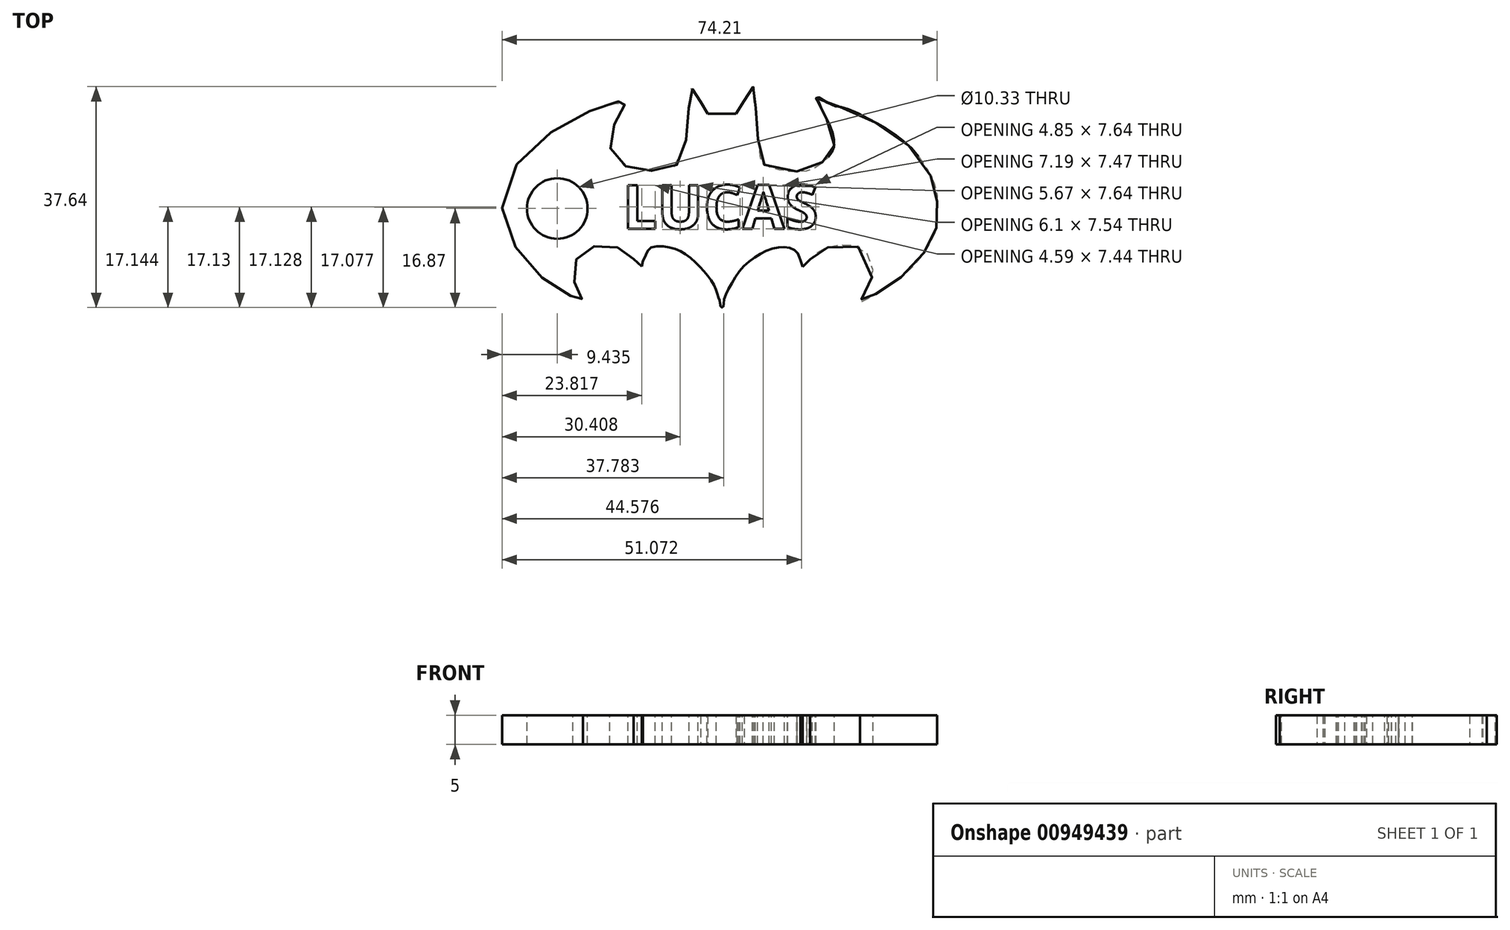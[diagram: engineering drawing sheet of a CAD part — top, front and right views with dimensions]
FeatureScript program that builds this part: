
annotation { "Feature Type Name" : "Feature", "Feature Type Description" : "" }
export const myFeature = defineFeature(function(context is Context, id is Id, definition is map)
    precondition{}
    {
        {
            var Q0;
            Q0=qCreatedBy(makeId("Top.planeOp"),FACE);
            var sketch = newSketch(context, id + "F0", { "sketchPlane" : qUnion([Q0])});
            skLineSegment(sketch, "E0", {"start": v(17.66, -46.63) * mm, "end": v(17.66, -46.63) * mm});
            skLineSegment(sketch, "E1", {"start": v(-27, -17.85) * mm, "end": v(-27.41, -19.78) * mm});
            skLineSegment(sketch, "E2", {"start": v(-27.41, -19.78) * mm, "end": v(-30.25, -17.16) * mm});
            skLineSegment(sketch, "E3", {"start": v(-7.41, 36.4) * mm, "end": v(-4.97, 32.28) * mm});
            skLineSegment(sketch, "E4", {"start": v(-4.97, 32.28) * mm, "end": v(-0.1, 32.28) * mm});
            skLineSegment(sketch, "E5", {"start": v(-0.1, 32.28) * mm, "end": v(4.75, 32.28) * mm});
            skLineSegment(sketch, "E6", {"start": v(4.75, 32.28) * mm, "end": v(7.5, 36.75) * mm});
            skLineSegment(sketch, "E7", {"start": v(30, -17.28) * mm, "end": v(27.37, -19.85) * mm});
            skLineSegment(sketch, "E8", {"start": v(27.37, -19.85) * mm, "end": v(26.62, -17.56) * mm});
            skFitSpline(sketch, "E9", {"points": [v(-0.67, -32.74) * mm, v(-0.72, -32.42) * mm, v(-0.87, -31.55) * mm, v(-1.37, -30.07) * mm, v(-2.33, -27.07) * mm, v(-4.94, -22.95) * mm, v(-9.05, -18.48) * mm, v(-14.03, -14.66) * mm, v(-19.36, -13.03) * mm, v(-24.89, -13.72) * mm, v(-26.32, -16.53) * mm, v(-27, -17.85) * mm]});
            skFitSpline(sketch, "E10", {"points": [v(-30.25, -17.16) * mm, v(-31.32, -16.23) * mm, v(-33.31, -14.5) * mm, v(-36.97, -12.95) * mm, v(-40.69, -12.62) * mm, v(-44.31, -13.01) * mm, v(-47.44, -14.64) * mm, v(-49.65, -17.2) * mm, v(-50.84, -20.46) * mm, v(-50.62, -24.2) * mm, v(-49.5, -27.18) * mm, v(-48.4, -29.54) * mm, v(-48.02, -30.57) * mm, v(-47.58, -31.82) * mm, v(-49.28, -30.8) * mm, v(-50.74, -30.2) * mm, v(-56.1, -27.22) * mm, v(-63.04, -22.25) * mm, v(-70.18, -13.6) * mm, v(-74.82, -3) * mm, v(-72.99, 10.16) * mm, v(-63.13, 22.49) * mm, v(-52.35, 29.54) * mm, v(-41.97, 34.29) * mm, v(-38.1, 34.92) * mm, v(-32.3, 38.2) * mm, v(-32.67, 36.4) * mm, v(-33.2, 35.53) * mm, v(-34.45, 33.52) * mm, v(-36.13, 30.4) * mm, v(-37.47, 26.28) * mm, v(-38.38, 22.42) * mm, v(-37.45, 18.9) * mm, v(-35.16, 16.14) * mm, v(-31.8, 13.79) * mm, v(-27.1, 12.95) * mm, v(-22.18, 12.98) * mm, v(-17.66, 13.92) * mm, v(-14.03, 16.16) * mm, v(-12.47, 21.01) * mm, v(-12.14, 27.18) * mm, v(-11.4, 34.27) * mm, v(-11.17, 37.8) * mm, v(-10.47, 40.95) * mm, v(-9.46, 39.55) * mm, v(-8.6, 38.36) * mm, v(-7.85, 37.1) * mm, v(-7.41, 36.4) * mm]});
            skFitSpline(sketch, "E11", {"points": [v(7.5, 36.75) * mm, v(8, 37.51) * mm, v(8.82, 38.82) * mm, v(9.65, 40.08) * mm, v(10.8, 41.53) * mm, v(10.58, 37.79) * mm, v(11.3, 35.16) * mm, v(11.59, 29.4) * mm, v(12.12, 24.17) * mm, v(12.7, 20.02) * mm, v(13.41, 15.78) * mm, v(18.9, 13.43) * mm, v(25.3, 12.64) * mm, v(30.97, 13.56) * mm, v(33.99, 15.64) * mm, v(35.43, 16.9) * mm, v(37.1, 18.74) * mm, v(38.2, 22) * mm, v(37.29, 26.83) * mm, v(35.45, 30.9) * mm, v(33.74, 34.33) * mm, v(33.03, 35.91) * mm, v(32.02, 38.08) * mm, v(37.64, 35.16) * mm, v(41.14, 34.44) * mm, v(49.27, 30.9) * mm, v(57.38, 26.28) * mm, v(65.7, 19.27) * mm, v(70.2, 12.7) * mm, v(72.62, 7.85) * mm, v(73.29, 4.1) * mm, v(73.16, -0.06) * mm, v(73.29, -4.23) * mm, v(72.62, -7.97) * mm, v(70.68, -11.85) * mm, v(67.75, -16.6) * mm, v(63.1, -21.63) * mm, v(58.28, -25.46) * mm, v(53.23, -28.82) * mm, v(50.78, -29.8) * mm, v(47.1, -32.52) * mm, v(47.5, -31.03) * mm, v(47.96, -30.06) * mm, v(49.6, -26.69) * mm, v(51.4, -21.29) * mm, v(48.02, -13.94) * mm, v(41.74, -12.45) * mm, v(36.8, -13) * mm, v(33.03, -14.55) * mm, v(31.05, -16.34) * mm, v(30, -17.28) * mm]});
            skFitSpline(sketch, "E12", {"points": [v(26.62, -17.56) * mm, v(26.27, -16.7) * mm, v(25.6, -15.05) * mm, v(23.13, -13.52) * mm, v(19.85, -13.21) * mm, v(15.83, -14.04) * mm, v(11.54, -16.33) * mm, v(7.47, -19.58) * mm, v(4.22, -23.85) * mm, v(1.82, -28) * mm, v(0.64, -31.17) * mm, v(0.55, -32.88) * mm, v(0.38, -33.43) * mm, v(-0.01, -33.74) * mm, v(-0.4, -33.55) * mm, v(-0.62, -33.2) * mm, v(-0.65, -32.9) * mm, v(-0.67, -32.74) * mm]});
            skSolve(sketch);
        }
        {
            var Q0;
            Q0=makeQuery(id+"F0.imprint","IMPRINT",FACE,{"disambiguationData":[TD([[makeQuery(id+"F0.imprint","IMPRINT",EDGE,{"derivedFrom":sQuery(id+"F0.wireOp",EDGE,"E1")}),-1.0]])]});
            extrude(context, id + "F1", {"entities" : qUnion([Q0]), "depth" : 10 * mm, "offsetDistance" : 25 * mm});
        }
        {
            var Q0;
            Q0=makeQuery(id+"F1.opExtrude","CAP_FACE",FACE,{"disambiguationData":[OSD([sQuery(id+"F0.wireOp",EDGE,"E1"),sQuery(id+"F0.wireOp",EDGE,"E2"),sQuery(id+"F0.wireOp",EDGE,"E3"),sQuery(id+"F0.wireOp",EDGE,"E4"),sQuery(id+"F0.wireOp",EDGE,"E5"),sQuery(id+"F0.wireOp",EDGE,"E6"),sQuery(id+"F0.wireOp",EDGE,"E7"),sQuery(id+"F0.wireOp",EDGE,"E8"),sQuery(id+"F0.wireOp",EDGE,"E9"),sQuery(id+"F0.wireOp",EDGE,"E10"),sQuery(id+"F0.wireOp",EDGE,"E11"),sQuery(id+"F0.wireOp",EDGE,"E12")])],"isStart":false});
            var sketch = newSketch(context, id + "F2", { "sketchPlane" : qUnion([Q0])});
            skText(sketch, "E13", { "text": "LUCAS", "fontName": "OpenSans-Bold.ttf"});
            const initialGuessF2  = {"E13": [-0.03395, -0.00692, 1, 0, 0.015]};
            skSetInitialGuess(sketch, initialGuessF2);
            skSolve(sketch);
        }
        {
            var Q0;
            Q0=makeQuery(id+"F2.imprint","IMPRINT",FACE,{"disambiguationData":[TD([[makeQuery(id+"F2.imprint","IMPRINT",EDGE,{"derivedFrom":sQuery(id+"F2.wireOp",EDGE,"E13.sketch_text.stroke-0")}),-1.0]])]});
            var Q1;
            Q1=makeQuery(id+"F2.imprint","IMPRINT",FACE,{"disambiguationData":[TD([[makeQuery(id+"F2.imprint","IMPRINT",EDGE,{"derivedFrom":sQuery(id+"F2.wireOp",EDGE,"E13.sketch_text.stroke-6")}),-1.0]])]});
            var Q2;
            Q2=makeQuery(id+"F2.imprint","IMPRINT",FACE,{"disambiguationData":[TD([[makeQuery(id+"F2.imprint","IMPRINT",EDGE,{"derivedFrom":sQuery(id+"F2.wireOp",EDGE,"E13.sketch_text.stroke-21")}),-1.0]])]});
            var Q3;
            Q3=makeQuery(id+"F2.imprint","IMPRINT",FACE,{"disambiguationData":[TD([[makeQuery(id+"F2.imprint","IMPRINT",EDGE,{"derivedFrom":sQuery(id+"F2.wireOp",EDGE,"E13.sketch_text.stroke-36")}),-1.0]])]});
            var Q4;
            Q4=makeQuery(id+"F2.imprint","IMPRINT",FACE,{"disambiguationData":[TD([[makeQuery(id+"F2.imprint","IMPRINT",EDGE,{"derivedFrom":sQuery(id+"F2.wireOp",EDGE,"E13.sketch_text.stroke-48")}),-1.0]])]});
            extrude(context, id + "F3", {"entities" : qUnion([Q0, Q1, Q2, Q3, Q4]), "operationType" : NewBodyOperationType.REMOVE, "oppositeDirection" : true, "depth" : 10 * mm, "offsetDistance" : 25 * mm});
        }
        {
            var Q0;
            {var subQ0=sQuery(id+"F0.wireOp",EDGE,"E10");var subQ1=sQuery(id+"F0.wireOp",EDGE,"E9");var subQ2=sQuery(id+"F0.wireOp",EDGE,"E8");var subQ3=sQuery(id+"F0.wireOp",EDGE,"E7");var subQ4=sQuery(id+"F0.wireOp",EDGE,"E6");var subQ5=sQuery(id+"F0.wireOp",EDGE,"E11");var subQ6=sQuery(id+"F0.wireOp",EDGE,"E1");var subQ7=sQuery(id+"F0.wireOp",EDGE,"E5");var subQ8=sQuery(id+"F0.wireOp",EDGE,"E4");var subQ9=sQuery(id+"F0.wireOp",EDGE,"E2");var subQ10=sQuery(id+"F0.wireOp",EDGE,"E3");var subQ11=sQuery(id+"F0.wireOp",EDGE,"E12");Q0=makeQuery(id+"F3.boolean.opBoolean","SPLIT",FACE,{"disambiguationData":[TD([makeQuery(id+"F1.opExtrude","SWEPT_FACE",FACE,{"disambiguationData":[OSD([subQ6])]})])],"derivedFrom":makeQuery(id+"F1.opExtrude","CAP_FACE",FACE,{"disambiguationData":[OSD([subQ6,subQ9,subQ10,subQ8,subQ7,subQ4,subQ3,subQ2,subQ1,subQ0,subQ5,subQ11])],"isStart":false})});}
            var sketch = newSketch(context, id + "F4", { "sketchPlane" : qUnion([Q0])});
            skCircle(sketch, "E14", {"center": v(-56.25, 0) * mm, "radius": 10.33 * mm});
            skSolve(sketch);
        }
        {
            var Q0;
            Q0=makeQuery(id+"F4.imprint","IMPRINT",FACE,{"disambiguationData":[TD([[makeQuery(id+"F4.imprint","IMPRINT",EDGE,{"derivedFrom":sQuery(id+"F4.wireOp",EDGE,"E14")}),1.0]])]});
            extrude(context, id + "F5", {"entities" : qUnion([Q0]), "operationType" : NewBodyOperationType.REMOVE, "oppositeDirection" : true, "depth" : 10 * mm, "offsetDistance" : 25 * mm});
        }
        {
            var Q0;
            Q0=makeQuery(id+"F3.boolean.opBoolean","SPLIT",BODY,{"disambiguationData":[OD(1.0)],"derivedFrom":makeQuery(id+"F1.opExtrude","SWEPT_BODY",BODY,{"disambiguationData":[OSD([sQuery(id+"F0.wireOp",EDGE,"E1"),sQuery(id+"F0.wireOp",EDGE,"E2"),sQuery(id+"F0.wireOp",EDGE,"E3"),sQuery(id+"F0.wireOp",EDGE,"E4"),sQuery(id+"F0.wireOp",EDGE,"E5"),sQuery(id+"F0.wireOp",EDGE,"E6"),sQuery(id+"F0.wireOp",EDGE,"E7"),sQuery(id+"F0.wireOp",EDGE,"E8"),sQuery(id+"F0.wireOp",EDGE,"E9"),sQuery(id+"F0.wireOp",EDGE,"E10"),sQuery(id+"F0.wireOp",EDGE,"E11"),sQuery(id+"F0.wireOp",EDGE,"E12")])]})});
            var Q1;
            Q1=makeQuery(id+"F3.boolean.opBoolean","SPLIT",BODY,{"disambiguationData":[OD(0.0)],"derivedFrom":makeQuery(id+"F1.opExtrude","SWEPT_BODY",BODY,{"disambiguationData":[OSD([sQuery(id+"F0.wireOp",EDGE,"E1"),sQuery(id+"F0.wireOp",EDGE,"E2"),sQuery(id+"F0.wireOp",EDGE,"E3"),sQuery(id+"F0.wireOp",EDGE,"E4"),sQuery(id+"F0.wireOp",EDGE,"E5"),sQuery(id+"F0.wireOp",EDGE,"E6"),sQuery(id+"F0.wireOp",EDGE,"E7"),sQuery(id+"F0.wireOp",EDGE,"E8"),sQuery(id+"F0.wireOp",EDGE,"E9"),sQuery(id+"F0.wireOp",EDGE,"E10"),sQuery(id+"F0.wireOp",EDGE,"E11"),sQuery(id+"F0.wireOp",EDGE,"E12")])]})});
            var Q2;
            Q2=qCreatedBy(makeId("Origin.pointOp"),VERTEX);
            transform(context, id + "F6", {"entities" : qUnion([Q0, Q1]), "transformType" : TransformType.SCALE_UNIFORMLY, "scale" : 0.5, "scalePoint" : qUnion([Q2]), "makeCopy" : false});
        }
    });
